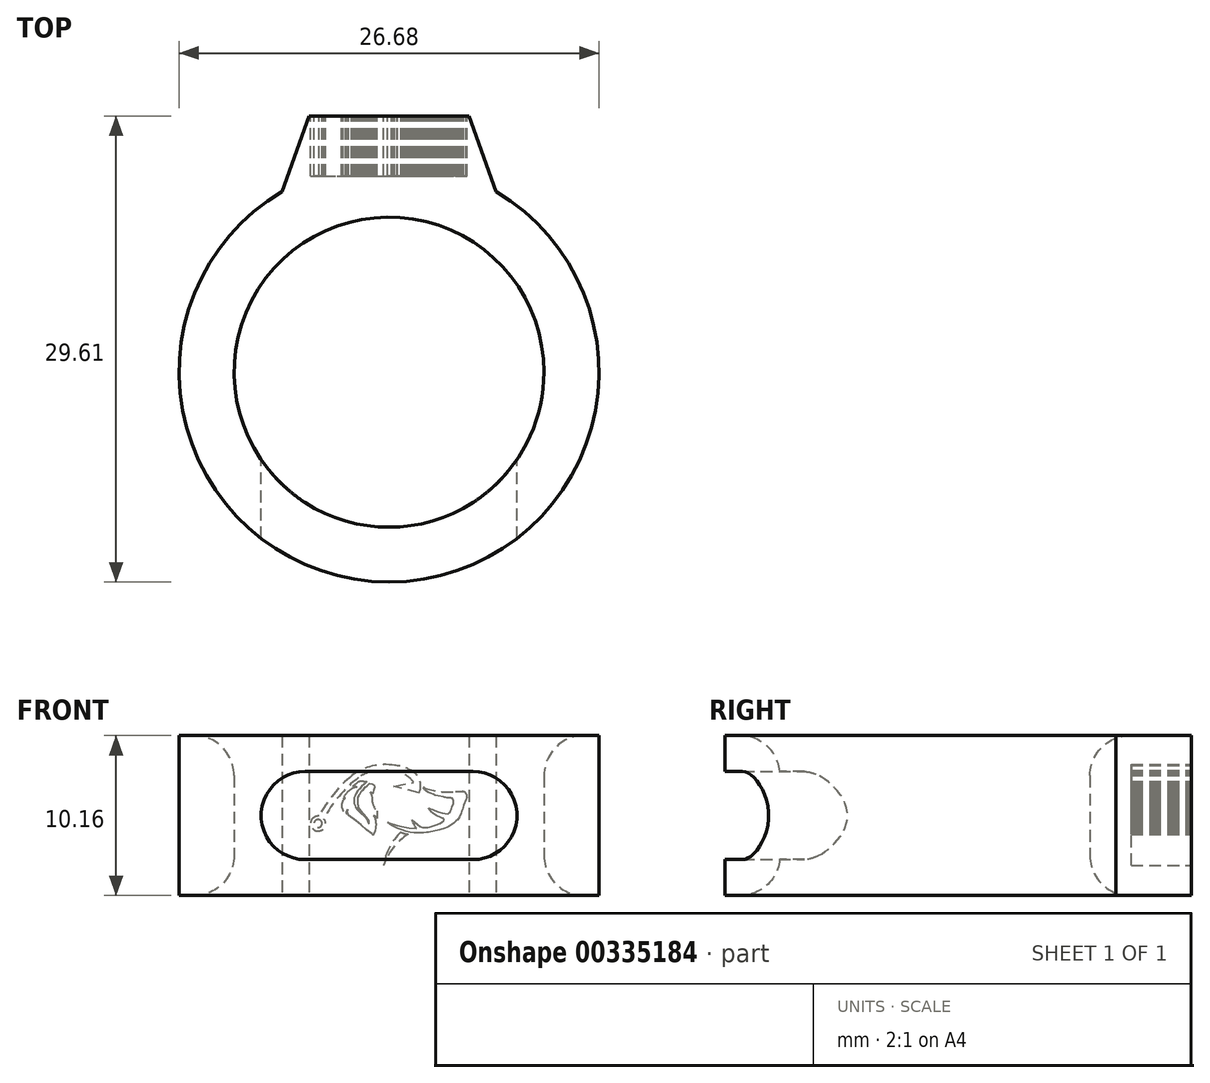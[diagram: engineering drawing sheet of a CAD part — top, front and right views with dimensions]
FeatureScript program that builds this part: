
annotation { "Feature Type Name" : "Feature", "Feature Type Description" : "" }
export const myFeature = defineFeature(function(context is Context, id is Id, definition is map)
    precondition{}
    {
        {
            var Q0;
            Q0=qCreatedBy(makeId("Top.planeOp"),FACE);
            var sketch = newSketch(context, id + "F0", { "sketchPlane" : qUnion([Q0])});
            skCircle(sketch, "E0", {"center": v(0, 0) * mm, "radius": 9.84 * mm});
            skCircle(sketch, "E1", {"center": v(0, 0) * mm, "radius": 13.34 * mm});
            skSolve(sketch);
        }
        {
            var Q0;
            Q0=makeQuery(id+"F0.imprint","IMPRINT",FACE,{"disambiguationData":[TD([[makeQuery(id+"F0.imprint","IMPRINT",EDGE,{"derivedFrom":sQuery(id+"F0.wireOp",EDGE,"E0")}),-1.0]])]});
            extrude(context, id + "F1", {"entities" : qUnion([Q0]), "endBound" : BoundingType.SYMMETRIC, "depth" : 10.16 * mm});
        }
        {
            var Q0;
            Q0=qCreatedBy(makeId("Front.planeOp"),FACE);
            var sketch = newSketch(context, id + "F2", { "sketchPlane" : qUnion([Q0])});
            skLineSegment(sketch, "E2", {"start": v(-5.33, 2.8) * mm, "end": v(5.33, 2.8) * mm});
            skLineSegment(sketch, "E3", {"start": v(-5.33, -2.8) * mm, "end": v(5.33, -2.8) * mm});
            skArc(sketch, "E4", {"start": v(5.33, -2.8) * mm, "mid": v(8.13, 0) * mm, "end": v(5.33, 2.8) * mm});
            skArc(sketch, "E5", {"start": v(-5.33, 2.8) * mm, "mid": v(-8.13, 0) * mm, "end": v(-5.33, -2.8) * mm});
            skSolve(sketch);
        }
        {
            var Q0;
            Q0=makeQuery(id+"F2.imprint","IMPRINT",FACE,{"disambiguationData":[TD([[makeQuery(id+"F2.imprint","IMPRINT",EDGE,{"derivedFrom":sQuery(id+"F2.wireOp",EDGE,"E2")}),-1.0]])]});
            extrude(context, id + "F3", {"entities" : qUnion([Q0]), "operationType" : NewBodyOperationType.REMOVE, "depth" : 25.4 * mm});
        }
        {
            var Q0;
            Q0=qCreatedBy(makeId("Top.planeOp"),FACE);
            var sketch = newSketch(context, id + "F4", { "sketchPlane" : qUnion([Q0])});
            skCircle(sketch, "E6.0", {"center": v(0, 0) * mm, "radius": 13.34 * mm});
            skLineSegment(sketch, "E7", {"start": v(-6.78, 11.48) * mm, "end": v(-5.08, 16.27) * mm});
            skLineSegment(sketch, "E8", {"start": v(-5.08, 16.27) * mm, "end": v(5.08, 16.27) * mm});
            skLineSegment(sketch, "E9", {"start": v(5.08, 16.27) * mm, "end": v(6.78, 11.48) * mm});
            skSolve(sketch);
        }
        {
            var Q0;
            {var subQ0=sQuery(id+"F4.wireOp",EDGE,"E7");Q0=makeQuery(id+"F4.imprint","IMPRINT",FACE,{"disambiguationData":[TD([[makeQuery(id+"F4.imprint","IMPRINT",EDGE,{"derivedFrom":subQ0}),-1.0]])]});}
            extrude(context, id + "F5", {"entities" : qUnion([Q0]), "operationType" : NewBodyOperationType.ADD, "endBound" : BoundingType.SYMMETRIC, "depth" : 10.16 * mm});
        }
        {
            var Q0;
            Q0=makeQuery(id+"F1.opExtrude","CAP_EDGE",EDGE,{"disambiguationData":[OSD([sQuery(id+"F0.wireOp",EDGE,"E0")])],"isStart":false});
            var Q1;
            Q1=makeQuery(id+"F1.opExtrude","CAP_EDGE",EDGE,{"disambiguationData":[OSD([sQuery(id+"F0.wireOp",EDGE,"E0")])],"isStart":true});
            fillet(context, id + "F6", {"entities" : qUnion([Q0, Q1]), "radius" : 2.54 * mm, "tangentPropagation" : true, "allowEdgeOverflow" : false});
        }
        {
            var Q0;
            Q0=makeQuery(id+"F5.opExtrude","SWEPT_FACE",FACE,{"disambiguationData":[OSD([sQuery(id+"F4.wireOp",EDGE,"E8")])]});
            var sketch = newSketch(context, id + "F7", { "sketchPlane" : qUnion([Q0])});
            skArc(sketch, "E10", {"start": v(-4.23, 1.52) * mm, "mid": v(-3.2, 1.53) * mm, "end": v(-2.2, 1.78) * mm});
            skLineSegment(sketch, "E11", {"start": v(-4.23, 1.52) * mm, "end": v(-4.52, 1.52) * mm});
            skLineSegment(sketch, "E12", {"start": v(-4.52, 1.52) * mm, "end": v(-4.66, 1.52) * mm});
            skArc(sketch, "E13", {"start": v(-4.66, 1.52) * mm, "mid": v(-4.9, 1.4) * mm, "end": v(-4.94, 1.15) * mm});
            skLineSegment(sketch, "E14", {"start": v(-4.94, 1.15) * mm, "end": v(-4.9, 1.03) * mm});
            skLineSegment(sketch, "E15", {"start": v(-4.9, 1.03) * mm, "end": v(-4.84, 0.9) * mm});
            skLineSegment(sketch, "E16", {"start": v(-4.84, 0.9) * mm, "end": v(-4.79, 0.78) * mm});
            skLineSegment(sketch, "E17", {"start": v(-4.79, 0.78) * mm, "end": v(-4.73, 0.65) * mm});
            skLineSegment(sketch, "E18", {"start": v(-4.73, 0.65) * mm, "end": v(-4.69, 0.52) * mm});
            skLineSegment(sketch, "E19", {"start": v(-4.69, 0.52) * mm, "end": v(-4.66, 0.4) * mm});
            skLineSegment(sketch, "E20", {"start": v(-4.66, 0.4) * mm, "end": v(-4.62, 0.28) * mm});
            skLineSegment(sketch, "E21", {"start": v(-4.62, 0.28) * mm, "end": v(-4.57, 0.15) * mm});
            skLineSegment(sketch, "E22", {"start": v(-4.57, 0.15) * mm, "end": v(-4.52, 0.02) * mm});
            skLineSegment(sketch, "E23", {"start": v(-4.52, 0.02) * mm, "end": v(-4.48, -0.1) * mm});
            skLineSegment(sketch, "E24", {"start": v(-4.48, -0.1) * mm, "end": v(-4.41, -0.17) * mm});
            skLineSegment(sketch, "E25", {"start": v(-4.41, -0.17) * mm, "end": v(-4.35, -0.26) * mm});
            skLineSegment(sketch, "E26", {"start": v(-4.35, -0.26) * mm, "end": v(-4.26, -0.35) * mm});
            skLineSegment(sketch, "E27", {"start": v(-4.26, -0.35) * mm, "end": v(-4.16, -0.44) * mm});
            skLineSegment(sketch, "E28", {"start": v(-4.16, -0.44) * mm, "end": v(-4.08, -0.5) * mm});
            skLineSegment(sketch, "E29", {"start": v(-4.08, -0.5) * mm, "end": v(-4, -0.57) * mm});
            skLineSegment(sketch, "E30", {"start": v(-4, -0.57) * mm, "end": v(-3.92, -0.62) * mm});
            skLineSegment(sketch, "E31", {"start": v(-3.92, -0.62) * mm, "end": v(-3.8, -0.69) * mm});
            skLineSegment(sketch, "E32", {"start": v(-3.8, -0.69) * mm, "end": v(-3.67, -0.75) * mm});
            skLineSegment(sketch, "E33", {"start": v(-3.67, -0.75) * mm, "end": v(-3.52, -0.8) * mm});
            skLineSegment(sketch, "E34", {"start": v(-3.52, -0.8) * mm, "end": v(-3.37, -0.86) * mm});
            skLineSegment(sketch, "E35", {"start": v(-3.37, -0.86) * mm, "end": v(-3.2, -0.91) * mm});
            skLineSegment(sketch, "E36", {"start": v(-3.2, -0.91) * mm, "end": v(-3.05, -0.95) * mm});
            skLineSegment(sketch, "E37", {"start": v(-3.05, -0.95) * mm, "end": v(-2.87, -0.99) * mm});
            skLineSegment(sketch, "E38", {"start": v(-2.87, -0.99) * mm, "end": v(-2.81, -1) * mm});
            skLineSegment(sketch, "E39", {"start": v(-2.81, -1) * mm, "end": v(-2.67, -1.03) * mm});
            skLineSegment(sketch, "E40", {"start": v(-2.67, -1.03) * mm, "end": v(-2.5, -1.06) * mm});
            skLineSegment(sketch, "E41", {"start": v(-2.5, -1.06) * mm, "end": v(-2.37, -1.08) * mm});
            skLineSegment(sketch, "E42", {"start": v(-2.37, -1.08) * mm, "end": v(-2.19, -1.1) * mm});
            skLineSegment(sketch, "E43", {"start": v(-2.19, -1.1) * mm, "end": v(-2, -1.1) * mm});
            skLineSegment(sketch, "E44", {"start": v(-2, -1.1) * mm, "end": v(-1.8, -1.1) * mm});
            skLineSegment(sketch, "E45", {"start": v(-1.8, -1.1) * mm, "end": v(-1.57, -1.1) * mm});
            skLineSegment(sketch, "E46", {"start": v(-1.57, -1.1) * mm, "end": v(-1.35, -1.06) * mm});
            skLineSegment(sketch, "E47", {"start": v(-1.35, -1.06) * mm, "end": v(-1.07, -1) * mm});
            skLineSegment(sketch, "E48", {"start": v(-1.07, -1) * mm, "end": v(-0.82, -0.92) * mm});
            skLineSegment(sketch, "E49", {"start": v(-0.82, -0.92) * mm, "end": v(-0.55, -0.82) * mm});
            skLineSegment(sketch, "E50", {"start": v(-0.55, -0.82) * mm, "end": v(-0.34, -0.72) * mm});
            skLineSegment(sketch, "E51", {"start": v(-0.34, -0.72) * mm, "end": v(-0.16, -0.61) * mm});
            skLineSegment(sketch, "E52", {"start": v(-0.16, -0.61) * mm, "end": v(0.1, -0.44) * mm});
            skLineSegment(sketch, "E53", {"start": v(0.1, -0.44) * mm, "end": v(-0.28, -0.56) * mm});
            skLineSegment(sketch, "E54", {"start": v(-0.28, -0.56) * mm, "end": v(-0.51, -0.62) * mm});
            skLineSegment(sketch, "E55", {"start": v(-0.51, -0.62) * mm, "end": v(-0.97, -0.72) * mm});
            skLineSegment(sketch, "E56", {"start": v(-0.97, -0.72) * mm, "end": v(-1.27, -0.77) * mm});
            skLineSegment(sketch, "E57", {"start": v(-1.27, -0.77) * mm, "end": v(-1.59, -0.8) * mm});
            skLineSegment(sketch, "E58", {"start": v(-1.59, -0.8) * mm, "end": v(-1.74, -0.8) * mm});
            skLineSegment(sketch, "E59", {"start": v(-1.74, -0.8) * mm, "end": v(-1.66, -0.7) * mm});
            skLineSegment(sketch, "E60", {"start": v(-1.66, -0.7) * mm, "end": v(-1.62, -0.63) * mm});
            skLineSegment(sketch, "E61", {"start": v(-1.62, -0.63) * mm, "end": v(-1.57, -0.53) * mm});
            skLineSegment(sketch, "E62", {"start": v(-1.57, -0.53) * mm, "end": v(-1.52, -0.42) * mm});
            skLineSegment(sketch, "E63", {"start": v(-1.52, -0.42) * mm, "end": v(-1.48, -0.32) * mm});
            skLineSegment(sketch, "E64", {"start": v(-1.48, -0.32) * mm, "end": v(-1.47, -0.28) * mm});
            skLineSegment(sketch, "E65", {"start": v(-1.47, -0.28) * mm, "end": v(-1.69, -0.46) * mm});
            skLineSegment(sketch, "E66", {"start": v(-1.69, -0.46) * mm, "end": v(-1.8, -0.56) * mm});
            skLineSegment(sketch, "E67", {"start": v(-1.8, -0.56) * mm, "end": v(-1.96, -0.67) * mm});
            skLineSegment(sketch, "E68", {"start": v(-1.96, -0.67) * mm, "end": v(-2.04, -0.72) * mm});
            skLineSegment(sketch, "E69", {"start": v(-2.04, -0.72) * mm, "end": v(-2.12, -0.75) * mm});
            skLineSegment(sketch, "E70", {"start": v(-2.12, -0.75) * mm, "end": v(-2.17, -0.76) * mm});
            skLineSegment(sketch, "E71", {"start": v(-2.17, -0.76) * mm, "end": v(-2.23, -0.76) * mm});
            skLineSegment(sketch, "E72", {"start": v(-2.23, -0.76) * mm, "end": v(-2.29, -0.76) * mm});
            skLineSegment(sketch, "E73", {"start": v(-2.29, -0.76) * mm, "end": v(-2.35, -0.76) * mm});
            skLineSegment(sketch, "E74", {"start": v(-2.35, -0.76) * mm, "end": v(-2.48, -0.74) * mm});
            skLineSegment(sketch, "E75", {"start": v(-2.48, -0.74) * mm, "end": v(-2.61, -0.72) * mm});
            skLineSegment(sketch, "E76", {"start": v(-2.61, -0.72) * mm, "end": v(-2.8, -0.67) * mm});
            skLineSegment(sketch, "E77", {"start": v(-2.8, -0.67) * mm, "end": v(-2.98, -0.6) * mm});
            skLineSegment(sketch, "E78", {"start": v(-2.98, -0.6) * mm, "end": v(-3.23, -0.49) * mm});
            skLineSegment(sketch, "E79", {"start": v(-3.23, -0.49) * mm, "end": v(-3.36, -0.4) * mm});
            skLineSegment(sketch, "E80", {"start": v(-3.36, -0.4) * mm, "end": v(-3.45, -0.33) * mm});
            skLineSegment(sketch, "E81", {"start": v(-3.45, -0.33) * mm, "end": v(-3.48, -0.28) * mm});
            skLineSegment(sketch, "E82", {"start": v(-3.48, -0.28) * mm, "end": v(-3.48, -0.26) * mm});
            skLineSegment(sketch, "E83", {"start": v(-3.48, -0.26) * mm, "end": v(-3.48, -0.23) * mm});
            skLineSegment(sketch, "E84", {"start": v(-3.48, -0.23) * mm, "end": v(-3.47, -0.21) * mm});
            skLineSegment(sketch, "E85", {"start": v(-3.47, -0.21) * mm, "end": v(-3.45, -0.2) * mm});
            skLineSegment(sketch, "E86", {"start": v(-3.45, -0.2) * mm, "end": v(-3.41, -0.18) * mm});
            skLineSegment(sketch, "E87", {"start": v(-3.41, -0.18) * mm, "end": v(-3.4, -0.16) * mm});
            skLineSegment(sketch, "E88", {"start": v(-3.4, -0.16) * mm, "end": v(-3.33, -0.14) * mm});
            skLineSegment(sketch, "E89", {"start": v(-3.33, -0.14) * mm, "end": v(-3.24, -0.1) * mm});
            skLineSegment(sketch, "E90", {"start": v(-3.24, -0.1) * mm, "end": v(-3.18, -0.07) * mm});
            skLineSegment(sketch, "E91", {"start": v(-3.18, -0.07) * mm, "end": v(-3.1, -0.03) * mm});
            skLineSegment(sketch, "E92", {"start": v(-3.1, -0.03) * mm, "end": v(-3, 0.02) * mm});
            skLineSegment(sketch, "E93", {"start": v(-3, 0.02) * mm, "end": v(-2.9, 0.08) * mm});
            skLineSegment(sketch, "E94", {"start": v(-2.9, 0.08) * mm, "end": v(-2.8, 0.15) * mm});
            skLineSegment(sketch, "E95", {"start": v(-2.8, 0.15) * mm, "end": v(-2.7, 0.25) * mm});
            skLineSegment(sketch, "E96", {"start": v(-2.7, 0.25) * mm, "end": v(-2.6, 0.37) * mm});
            skLineSegment(sketch, "E97", {"start": v(-2.6, 0.37) * mm, "end": v(-2.53, 0.46) * mm});
            skLineSegment(sketch, "E98", {"start": v(-2.53, 0.46) * mm, "end": v(-2.52, 0.47) * mm});
            skLineSegment(sketch, "E99", {"start": v(-2.52, 0.47) * mm, "end": v(-2.64, 0.43) * mm});
            skLineSegment(sketch, "E100", {"start": v(-2.64, 0.43) * mm, "end": v(-2.75, 0.38) * mm});
            skLineSegment(sketch, "E101", {"start": v(-2.75, 0.38) * mm, "end": v(-2.9, 0.32) * mm});
            skLineSegment(sketch, "E102", {"start": v(-2.9, 0.32) * mm, "end": v(-3.14, 0.22) * mm});
            skLineSegment(sketch, "E103", {"start": v(-3.14, 0.22) * mm, "end": v(-3.36, 0.17) * mm});
            skLineSegment(sketch, "E104", {"start": v(-3.36, 0.17) * mm, "end": v(-3.62, 0.14) * mm});
            skLineSegment(sketch, "E105", {"start": v(-3.62, 0.14) * mm, "end": v(-3.75, 0.12) * mm});
            skLineSegment(sketch, "E106", {"start": v(-3.75, 0.12) * mm, "end": v(-3.83, 0.17) * mm});
            skLineSegment(sketch, "E107", {"start": v(-3.83, 0.17) * mm, "end": v(-3.87, 0.22) * mm});
            skLineSegment(sketch, "E108", {"start": v(-3.87, 0.22) * mm, "end": v(-3.91, 0.28) * mm});
            skLineSegment(sketch, "E109", {"start": v(-3.91, 0.28) * mm, "end": v(-3.98, 0.43) * mm});
            skLineSegment(sketch, "E110", {"start": v(-3.98, 0.43) * mm, "end": v(-4.02, 0.55) * mm});
            skLineSegment(sketch, "E111", {"start": v(-4.02, 0.55) * mm, "end": v(-4.07, 0.7) * mm});
            skLineSegment(sketch, "E112", {"start": v(-4.07, 0.7) * mm, "end": v(-4.1, 0.76) * mm});
            skLineSegment(sketch, "E113", {"start": v(-4.1, 0.76) * mm, "end": v(-4.1, 0.84) * mm});
            skLineSegment(sketch, "E114", {"start": v(-4.1, 0.84) * mm, "end": v(-4.11, 0.9) * mm});
            skLineSegment(sketch, "E115", {"start": v(-4.11, 0.9) * mm, "end": v(-4.1, 0.94) * mm});
            skLineSegment(sketch, "E116", {"start": v(-4.1, 0.94) * mm, "end": v(-4.1, 0.98) * mm});
            skLineSegment(sketch, "E117", {"start": v(-4.1, 0.98) * mm, "end": v(-4.08, 1.01) * mm});
            skLineSegment(sketch, "E118", {"start": v(-4.08, 1.01) * mm, "end": v(-4.06, 1.04) * mm});
            skLineSegment(sketch, "E119", {"start": v(-4.06, 1.04) * mm, "end": v(-4.02, 1.08) * mm});
            skLineSegment(sketch, "E120", {"start": v(-4.02, 1.08) * mm, "end": v(-3.98, 1.1) * mm});
            skLineSegment(sketch, "E121", {"start": v(-3.98, 1.1) * mm, "end": v(-3.94, 1.1) * mm});
            skLineSegment(sketch, "E122", {"start": v(-3.94, 1.1) * mm, "end": v(-3.89, 1.1) * mm});
            skLineSegment(sketch, "E123", {"start": v(-3.89, 1.1) * mm, "end": v(-3.83, 1.1) * mm});
            skLineSegment(sketch, "E124", {"start": v(-3.83, 1.1) * mm, "end": v(-3.75, 1.12) * mm});
            skLineSegment(sketch, "E125", {"start": v(-3.75, 1.12) * mm, "end": v(-3.68, 1.13) * mm});
            skLineSegment(sketch, "E126", {"start": v(-3.68, 1.13) * mm, "end": v(-3.6, 1.15) * mm});
            skLineSegment(sketch, "E127", {"start": v(-3.6, 1.15) * mm, "end": v(-3.53, 1.16) * mm});
            skLineSegment(sketch, "E128", {"start": v(-3.53, 1.16) * mm, "end": v(-3.45, 1.18) * mm});
            skLineSegment(sketch, "E129", {"start": v(-3.45, 1.18) * mm, "end": v(-3.34, 1.2) * mm});
            skLineSegment(sketch, "E130", {"start": v(-3.34, 1.2) * mm, "end": v(-3.27, 1.21) * mm});
            skLineSegment(sketch, "E131", {"start": v(-3.27, 1.21) * mm, "end": v(-3.1, 1.24) * mm});
            skLineSegment(sketch, "E132", {"start": v(-3.1, 1.24) * mm, "end": v(-2.93, 1.3) * mm});
            skLineSegment(sketch, "E133", {"start": v(-2.93, 1.3) * mm, "end": v(-2.83, 1.33) * mm});
            skLineSegment(sketch, "E134", {"start": v(-2.83, 1.33) * mm, "end": v(-2.66, 1.4) * mm});
            skLineSegment(sketch, "E135", {"start": v(-2.66, 1.4) * mm, "end": v(-2.5, 1.48) * mm});
            skLineSegment(sketch, "E136", {"start": v(-2.5, 1.48) * mm, "end": v(-2.35, 1.57) * mm});
            skLineSegment(sketch, "E137", {"start": v(-2.35, 1.57) * mm, "end": v(-2.26, 1.64) * mm});
            skLineSegment(sketch, "E138", {"start": v(-2.26, 1.64) * mm, "end": v(-2.22, 1.7) * mm});
            skLineSegment(sketch, "E139", {"start": v(-2.22, 1.7) * mm, "end": v(-2.2, 1.74) * mm});
            skLineSegment(sketch, "E140", {"start": v(-2.2, 1.74) * mm, "end": v(-2.2, 1.76) * mm});
            skLineSegment(sketch, "E141", {"start": v(-2.2, 1.78) * mm, "end": v(-2.2, 1.78) * mm});
            skLineSegment(sketch, "E142", {"start": v(-2.2, 1.78) * mm, "end": v(-2.2, 1.76) * mm});
            skLineSegment(sketch, "E143", {"start": v(-1.92, 1.45) * mm, "end": v(-0.3, 1.86) * mm});
            skLineSegment(sketch, "E144", {"start": v(-0.3, 1.86) * mm, "end": v(-1.56, 2.1) * mm});
            skArc(sketch, "E145", {"start": v(-1.7, 2.64) * mm, "mid": v(-2, 2.08) * mm, "end": v(-1.92, 1.45) * mm});
            skArc(sketch, "E146", {"start": v(-0.36, 3.18) * mm, "mid": v(-1.08, 3.02) * mm, "end": v(-1.7, 2.64) * mm});
            skArc(sketch, "E147", {"start": v(2.36, 2.54) * mm, "mid": v(1.07, 3.14) * mm, "end": v(-0.36, 3.18) * mm});
            skArc(sketch, "E148", {"start": v(4.46, -0.03) * mm, "mid": v(3.53, 1.35) * mm, "end": v(2.36, 2.54) * mm});
            skArc(sketch, "E149", {"start": v(4.14, -0.2) * mm, "mid": v(4.73, -0.93) * mm, "end": v(4.46, -0.03) * mm});
            skArc(sketch, "E150", {"start": v(-0.55, 2.78) * mm, "mid": v(-1.12, 2.54) * mm, "end": v(-1.56, 2.1) * mm});
            skArc(sketch, "E151", {"start": v(1.1, 2.78) * mm, "mid": v(0.28, 2.86) * mm, "end": v(-0.55, 2.78) * mm});
            skArc(sketch, "E152", {"start": v(1.94, 2.41) * mm, "mid": v(1.54, 2.65) * mm, "end": v(1.1, 2.78) * mm});
            skArc(sketch, "E153", {"start": v(4.14, -0.2) * mm, "mid": v(3.18, 1.22) * mm, "end": v(1.94, 2.41) * mm});
            skCircle(sketch, "E154", {"center": v(4.5, -0.5) * mm, "radius": 0.25 * mm});
            skArc(sketch, "E155", {"start": v(0.35, -3.16) * mm, "mid": v(-0.27, -2.04) * mm, "end": v(-1.2, -1.18) * mm});
            skPoint(sketch, "E155.endSnap0", {"position": v(-1.2, -1.03) * mm});
            skArc(sketch, "E156", {"start": v(0.35, -3.16) * mm, "mid": v(-0.03, -2.01) * mm, "end": v(-0.75, -1.04) * mm});
            skArc(sketch, "E157", {"start": v(-1.2, -1.18) * mm, "mid": v(-0.97, -1.14) * mm, "end": v(-0.75, -1.04) * mm});
            skLineSegment(sketch, "E158", {"start": v(0.7, 2.45) * mm, "end": v(0.75, 2.5) * mm});
            skLineSegment(sketch, "E159", {"start": v(0.75, 2.5) * mm, "end": v(0.88, 2.45) * mm});
            skLineSegment(sketch, "E160", {"start": v(0.88, 2.45) * mm, "end": v(1, 2.37) * mm});
            skLineSegment(sketch, "E161", {"start": v(1, 2.37) * mm, "end": v(1.12, 2.3) * mm});
            skLineSegment(sketch, "E162", {"start": v(1.12, 2.3) * mm, "end": v(1.24, 2.21) * mm});
            skLineSegment(sketch, "E163", {"start": v(1.24, 2.21) * mm, "end": v(1.36, 2.12) * mm});
            skLineSegment(sketch, "E164", {"start": v(1.36, 2.12) * mm, "end": v(1.5, 2) * mm});
            skLineSegment(sketch, "E165", {"start": v(1.5, 2) * mm, "end": v(1.6, 1.9) * mm});
            skLineSegment(sketch, "E166", {"start": v(1.6, 1.9) * mm, "end": v(1.72, 1.8) * mm});
            skLineSegment(sketch, "E167", {"start": v(1.72, 1.8) * mm, "end": v(1.83, 1.68) * mm});
            skLineSegment(sketch, "E168", {"start": v(1.83, 1.68) * mm, "end": v(1.9, 1.58) * mm});
            skLineSegment(sketch, "E169", {"start": v(1.9, 1.58) * mm, "end": v(1.98, 1.49) * mm});
            skLineSegment(sketch, "E170", {"start": v(1.98, 1.49) * mm, "end": v(2.05, 1.38) * mm});
            skLineSegment(sketch, "E171", {"start": v(2.05, 1.38) * mm, "end": v(2.1, 1.29) * mm});
            skLineSegment(sketch, "E172", {"start": v(2.1, 1.29) * mm, "end": v(2.15, 1.18) * mm});
            skLineSegment(sketch, "E173", {"start": v(2.15, 1.18) * mm, "end": v(2.17, 1.08) * mm});
            skLineSegment(sketch, "E174", {"start": v(2.17, 1.08) * mm, "end": v(2.18, 0.93) * mm});
            skLineSegment(sketch, "E175", {"start": v(2.18, 0.93) * mm, "end": v(2.17, 0.78) * mm});
            skLineSegment(sketch, "E176", {"start": v(2.17, 0.78) * mm, "end": v(2.12, 0.63) * mm});
            skLineSegment(sketch, "E177", {"start": v(2.12, 0.63) * mm, "end": v(2.06, 0.52) * mm});
            skLineSegment(sketch, "E178", {"start": v(2.06, 0.52) * mm, "end": v(1.97, 0.4) * mm});
            skLineSegment(sketch, "E179", {"start": v(1.97, 0.4) * mm, "end": v(1.75, 0.17) * mm});
            skLineSegment(sketch, "E180", {"start": v(1.75, 0.17) * mm, "end": v(1.92, 0.44) * mm});
            skLineSegment(sketch, "E181", {"start": v(1.92, 0.44) * mm, "end": v(1.96, 0.53) * mm});
            skLineSegment(sketch, "E182", {"start": v(1.96, 0.53) * mm, "end": v(1.98, 0.62) * mm});
            skLineSegment(sketch, "E183", {"start": v(1.98, 0.62) * mm, "end": v(2, 0.7) * mm});
            skLineSegment(sketch, "E184", {"start": v(2, 0.7) * mm, "end": v(2.01, 0.77) * mm});
            skLineSegment(sketch, "E185", {"start": v(2.01, 0.77) * mm, "end": v(2.01, 0.87) * mm});
            skLineSegment(sketch, "E186", {"start": v(2.01, 0.87) * mm, "end": v(2.01, 0.99) * mm});
            skLineSegment(sketch, "E187", {"start": v(2.01, 0.99) * mm, "end": v(2, 1.08) * mm});
            skLineSegment(sketch, "E188", {"start": v(2, 1.08) * mm, "end": v(2, 1.14) * mm});
            skLineSegment(sketch, "E189", {"start": v(2, 1.14) * mm, "end": v(1.98, 1.19) * mm});
            skLineSegment(sketch, "E190", {"start": v(1.98, 1.19) * mm, "end": v(1.95, 1.27) * mm});
            skLineSegment(sketch, "E191", {"start": v(1.95, 1.27) * mm, "end": v(1.89, 1.39) * mm});
            skLineSegment(sketch, "E192", {"start": v(1.89, 1.39) * mm, "end": v(1.81, 1.51) * mm});
            skLineSegment(sketch, "E193", {"start": v(1.81, 1.51) * mm, "end": v(1.76, 1.58) * mm});
            skLineSegment(sketch, "E194", {"start": v(1.76, 1.58) * mm, "end": v(1.68, 1.67) * mm});
            skLineSegment(sketch, "E195", {"start": v(1.68, 1.67) * mm, "end": v(1.6, 1.76) * mm});
            skLineSegment(sketch, "E196", {"start": v(1.6, 1.76) * mm, "end": v(1.48, 1.89) * mm});
            skLineSegment(sketch, "E197", {"start": v(1.48, 1.89) * mm, "end": v(1.38, 1.97) * mm});
            skLineSegment(sketch, "E198", {"start": v(1.38, 1.97) * mm, "end": v(1.22, 2.1) * mm});
            skLineSegment(sketch, "E199", {"start": v(1.22, 2.1) * mm, "end": v(1.04, 2.23) * mm});
            skLineSegment(sketch, "E200", {"start": v(1.04, 2.23) * mm, "end": v(0.89, 2.32) * mm});
            skLineSegment(sketch, "E201", {"start": v(0.89, 2.32) * mm, "end": v(0.7, 2.45) * mm});
            skArc(sketch, "E202", {"start": v(2.03, 2.08) * mm, "mid": v(1.84, 2.17) * mm, "end": v(1.62, 2.17) * mm});
            skLineSegment(sketch, "E203", {"start": v(1.62, 2.17) * mm, "end": v(1.4, 2.17) * mm});
            skLineSegment(sketch, "E204", {"start": v(1.4, 2.17) * mm, "end": v(1.6, 1.99) * mm});
            skLineSegment(sketch, "E205", {"start": v(1.6, 1.99) * mm, "end": v(1.73, 1.86) * mm});
            skLineSegment(sketch, "E206", {"start": v(1.73, 1.86) * mm, "end": v(1.87, 1.7) * mm});
            skLineSegment(sketch, "E207", {"start": v(1.87, 1.7) * mm, "end": v(1.99, 1.55) * mm});
            skLineSegment(sketch, "E208", {"start": v(1.99, 1.55) * mm, "end": v(2.09, 1.41) * mm});
            skLineSegment(sketch, "E209", {"start": v(2.09, 1.41) * mm, "end": v(2.16, 1.26) * mm});
            skLineSegment(sketch, "E210", {"start": v(2.16, 1.26) * mm, "end": v(2.2, 1.18) * mm});
            skLineSegment(sketch, "E211", {"start": v(2.2, 1.18) * mm, "end": v(2.2, 1.12) * mm});
            skLineSegment(sketch, "E212", {"start": v(2.2, 1.12) * mm, "end": v(2.22, 1.05) * mm});
            skLineSegment(sketch, "E213", {"start": v(2.22, 1.05) * mm, "end": v(2.22, 0.96) * mm});
            skLineSegment(sketch, "E214", {"start": v(2.22, 0.96) * mm, "end": v(2.22, 0.89) * mm});
            skLineSegment(sketch, "E215", {"start": v(2.22, 0.89) * mm, "end": v(2.21, 0.78) * mm});
            skLineSegment(sketch, "E216", {"start": v(2.21, 0.78) * mm, "end": v(2.17, 0.64) * mm});
            skLineSegment(sketch, "E217", {"start": v(2.17, 0.64) * mm, "end": v(2.12, 0.51) * mm});
            skLineSegment(sketch, "E218", {"start": v(2.12, 0.51) * mm, "end": v(2.03, 0.4) * mm});
            skLineSegment(sketch, "E219", {"start": v(2.03, 0.4) * mm, "end": v(1.81, 0.17) * mm});
            skLineSegment(sketch, "E220", {"start": v(1.81, 0.17) * mm, "end": v(1.52, -0.1) * mm});
            skLineSegment(sketch, "E221", {"start": v(1.52, -0.1) * mm, "end": v(1.43, -0.21) * mm});
            skLineSegment(sketch, "E222", {"start": v(1.43, -0.21) * mm, "end": v(1.35, -0.33) * mm});
            skLineSegment(sketch, "E223", {"start": v(1.35, -0.33) * mm, "end": v(1.29, -0.49) * mm});
            skLineSegment(sketch, "E224", {"start": v(1.29, -0.49) * mm, "end": v(1.26, -0.54) * mm});
            skLineSegment(sketch, "E225", {"start": v(1.26, -0.54) * mm, "end": v(1.26, -0.45) * mm});
            skLineSegment(sketch, "E226", {"start": v(1.26, -0.45) * mm, "end": v(1.28, -0.35) * mm});
            skLineSegment(sketch, "E227", {"start": v(1.28, -0.35) * mm, "end": v(1.34, -0.24) * mm});
            skLineSegment(sketch, "E228", {"start": v(1.34, -0.24) * mm, "end": v(1.43, -0.12) * mm});
            skLineSegment(sketch, "E229", {"start": v(1.43, -0.12) * mm, "end": v(1.53, 0) * mm});
            skLineSegment(sketch, "E230", {"start": v(1.53, 0) * mm, "end": v(1.62, 0.1) * mm});
            skLineSegment(sketch, "E231", {"start": v(1.62, 0.1) * mm, "end": v(1.7, 0.2) * mm});
            skLineSegment(sketch, "E232", {"start": v(1.7, 0.2) * mm, "end": v(1.78, 0.31) * mm});
            skLineSegment(sketch, "E233", {"start": v(1.78, 0.31) * mm, "end": v(1.88, 0.47) * mm});
            skLineSegment(sketch, "E234", {"start": v(1.88, 0.47) * mm, "end": v(1.93, 0.54) * mm});
            skLineSegment(sketch, "E235", {"start": v(1.93, 0.54) * mm, "end": v(1.95, 0.62) * mm});
            skLineSegment(sketch, "E236", {"start": v(1.95, 0.62) * mm, "end": v(1.96, 0.7) * mm});
            skLineSegment(sketch, "E237", {"start": v(1.96, 0.7) * mm, "end": v(1.97, 0.8) * mm});
            skLineSegment(sketch, "E238", {"start": v(1.97, 0.8) * mm, "end": v(1.97, 0.92) * mm});
            skLineSegment(sketch, "E239", {"start": v(1.97, 0.92) * mm, "end": v(1.96, 1.1) * mm});
            skLineSegment(sketch, "E240", {"start": v(1.96, 1.1) * mm, "end": v(1.95, 1.16) * mm});
            skLineSegment(sketch, "E241", {"start": v(1.95, 1.16) * mm, "end": v(1.93, 1.21) * mm});
            skLineSegment(sketch, "E242", {"start": v(1.93, 1.21) * mm, "end": v(1.92, 1.26) * mm});
            skLineSegment(sketch, "E243", {"start": v(1.92, 1.26) * mm, "end": v(1.89, 1.3) * mm});
            skLineSegment(sketch, "E244", {"start": v(1.89, 1.3) * mm, "end": v(1.85, 1.37) * mm});
            skLineSegment(sketch, "E245", {"start": v(1.85, 1.37) * mm, "end": v(1.8, 1.45) * mm});
            skLineSegment(sketch, "E246", {"start": v(1.8, 1.45) * mm, "end": v(1.73, 1.56) * mm});
            skLineSegment(sketch, "E247", {"start": v(1.73, 1.56) * mm, "end": v(1.63, 1.67) * mm});
            skLineSegment(sketch, "E248", {"start": v(1.63, 1.67) * mm, "end": v(1.5, 1.8) * mm});
            skLineSegment(sketch, "E249", {"start": v(1.5, 1.8) * mm, "end": v(1.4, 1.9) * mm});
            skLineSegment(sketch, "E250", {"start": v(1.4, 1.9) * mm, "end": v(1.29, 1.98) * mm});
            skLineSegment(sketch, "E251", {"start": v(1.29, 1.98) * mm, "end": v(1.24, 2.04) * mm});
            skLineSegment(sketch, "E252", {"start": v(1.24, 2.04) * mm, "end": v(1.1, 2.02) * mm});
            skLineSegment(sketch, "E253", {"start": v(1.1, 2.02) * mm, "end": v(1, 1.98) * mm});
            skLineSegment(sketch, "E254", {"start": v(1, 1.98) * mm, "end": v(0.97, 1.96) * mm});
            skLineSegment(sketch, "E255", {"start": v(0.97, 1.96) * mm, "end": v(0.96, 1.94) * mm});
            skLineSegment(sketch, "E256", {"start": v(0.96, 1.94) * mm, "end": v(0.94, 1.9) * mm});
            skLineSegment(sketch, "E257", {"start": v(0.94, 1.9) * mm, "end": v(0.93, 1.85) * mm});
            skLineSegment(sketch, "E258", {"start": v(0.93, 1.85) * mm, "end": v(0.93, 1.79) * mm});
            skLineSegment(sketch, "E259", {"start": v(0.93, 1.79) * mm, "end": v(0.95, 1.7) * mm});
            skLineSegment(sketch, "E260", {"start": v(0.95, 1.7) * mm, "end": v(0.98, 1.6) * mm});
            skLineSegment(sketch, "E261", {"start": v(0.98, 1.6) * mm, "end": v(1.01, 1.47) * mm});
            skLineSegment(sketch, "E262", {"start": v(1.01, 1.47) * mm, "end": v(1.04, 1.39) * mm});
            skArc(sketch, "E263", {"start": v(1.18, 1.47) * mm, "mid": v(1.1, 1.45) * mm, "end": v(1.04, 1.39) * mm});
            skArc(sketch, "E264", {"start": v(1.18, 1.47) * mm, "mid": v(1.13, 1.4) * mm, "end": v(1.1, 1.3) * mm});
            skLineSegment(sketch, "E265", {"start": v(1.1, 1.3) * mm, "end": v(1.08, 1.1) * mm});
            skArc(sketch, "E266", {"start": v(0.78, 0.3) * mm, "mid": v(1, 0.67) * mm, "end": v(1.08, 1.1) * mm});
            skLineSegment(sketch, "E267", {"start": v(0.78, 0.3) * mm, "end": v(0.76, 0.25) * mm});
            skLineSegment(sketch, "E268", {"start": v(0.76, 0.25) * mm, "end": v(0.75, 0.21) * mm});
            skLineSegment(sketch, "E269", {"start": v(0.75, 0.21) * mm, "end": v(0.75, 0.15) * mm});
            skLineSegment(sketch, "E270", {"start": v(0.75, 0.15) * mm, "end": v(0.75, 0.08) * mm});
            skLineSegment(sketch, "E271", {"start": v(0.75, 0.08) * mm, "end": v(0.75, 0) * mm});
            skLineSegment(sketch, "E272", {"start": v(0.75, 0) * mm, "end": v(0.78, -0.17) * mm});
            skArc(sketch, "E273", {"start": v(0.97, -0.02) * mm, "mid": v(0.86, -0.07) * mm, "end": v(0.78, -0.17) * mm});
            skArc(sketch, "E274", {"start": v(0.97, -0.02) * mm, "mid": v(0.9, -0.13) * mm, "end": v(0.84, -0.25) * mm});
            skArc(sketch, "E275", {"start": v(0.84, -0.25) * mm, "mid": v(0.82, -0.37) * mm, "end": v(0.82, -0.49) * mm});
            skLineSegment(sketch, "E276", {"start": v(0.82, -0.49) * mm, "end": v(0.87, -0.78) * mm});
            skLineSegment(sketch, "E277", {"start": v(0.87, -0.78) * mm, "end": v(0.9, -0.98) * mm});
            skLineSegment(sketch, "E278", {"start": v(0.9, -0.98) * mm, "end": v(0.94, -1.14) * mm});
            skArc(sketch, "E279", {"start": v(0.94, -1.14) * mm, "mid": v(1, -1.2) * mm, "end": v(1.08, -1.18) * mm});
            skLineSegment(sketch, "E280", {"start": v(1.08, -1.18) * mm, "end": v(1.43, -0.9) * mm});
            skLineSegment(sketch, "E281", {"start": v(1.43, -0.9) * mm, "end": v(1.79, -0.6) * mm});
            skLineSegment(sketch, "E282", {"start": v(1.79, -0.6) * mm, "end": v(2.09, -0.35) * mm});
            skLineSegment(sketch, "E283", {"start": v(2.09, -0.35) * mm, "end": v(2.35, -0.15) * mm});
            skLineSegment(sketch, "E284", {"start": v(2.35, -0.15) * mm, "end": v(2.56, 0) * mm});
            skArc(sketch, "E285", {"start": v(2.56, 0) * mm, "mid": v(2.65, 0.19) * mm, "end": v(2.62, 0.4) * mm});
            skArc(sketch, "E286", {"start": v(2.7, 0.11) * mm, "mid": v(2.71, 0.27) * mm, "end": v(2.62, 0.4) * mm});
            skArc(sketch, "E287", {"start": v(2.7, 0.11) * mm, "mid": v(3, 0.5) * mm, "end": v(2.9, 0.98) * mm});
            skArc(sketch, "E288", {"start": v(2.9, 1.07) * mm, "mid": v(2.84, 1.1) * mm, "end": v(2.76, 1.1) * mm});
            skArc(sketch, "E289", {"start": v(2.9, 1.07) * mm, "mid": v(2.7, 1.42) * mm, "end": v(2.38, 1.69) * mm});
            skArc(sketch, "E290", {"start": v(2.38, 1.69) * mm, "mid": v(2.2, 1.77) * mm, "end": v(2.02, 1.8) * mm});
            skArc(sketch, "E291", {"start": v(2.28, 1.83) * mm, "mid": v(2.15, 1.84) * mm, "end": v(2.02, 1.8) * mm});
            skLineSegment(sketch, "E292", {"start": v(2.28, 1.83) * mm, "end": v(2.21, 1.93) * mm});
            skLineSegment(sketch, "E293", {"start": v(2.21, 1.93) * mm, "end": v(2.14, 2) * mm});
            skLineSegment(sketch, "E294", {"start": v(2.14, 2) * mm, "end": v(2.06, 2.05) * mm});
            skLineSegment(sketch, "E295", {"start": v(2.03, 2.08) * mm, "end": v(2.06, 2.05) * mm});
            skArc(sketch, "E296", {"start": v(2.9, 0.98) * mm, "mid": v(2.85, 1.06) * mm, "end": v(2.76, 1.1) * mm});
            skSolve(sketch);
        }
        {
            var Q0;
            Q0=makeQuery(id+"F7.imprint","IMPRINT",FACE,{"disambiguationData":[TD([[makeQuery(id+"F7.imprint","IMPRINT",EDGE,{"derivedFrom":sQuery(id+"F7.wireOp",EDGE,"E143")}),1.0]])]});
            var Q1;
            Q1=makeQuery(id+"F7.imprint","IMPRINT",FACE,{"disambiguationData":[TD([[makeQuery(id+"F7.imprint","IMPRINT",EDGE,{"derivedFrom":sQuery(id+"F7.wireOp",EDGE,"E10")}),-1.0]])]});
            var Q2;
            Q2=makeQuery(id+"F7.imprint","IMPRINT",FACE,{"disambiguationData":[TD([[makeQuery(id+"F7.imprint","IMPRINT",EDGE,{"derivedFrom":sQuery(id+"F7.wireOp",EDGE,"E155")}),-1.0]])]});
            var Q3;
            Q3=makeQuery(id+"F7.imprint","IMPRINT",FACE,{"disambiguationData":[TD([[makeQuery(id+"F7.imprint","IMPRINT",EDGE,{"derivedFrom":sQuery(id+"F7.wireOp",EDGE,"E202")}),1.0]])]});
            extrude(context, id + "F8", {"entities" : qUnion([Q0, Q1, Q2, Q3]), "operationType" : NewBodyOperationType.REMOVE, "oppositeDirection" : true, "depth" : 3.8 * mm});
        }
    });
